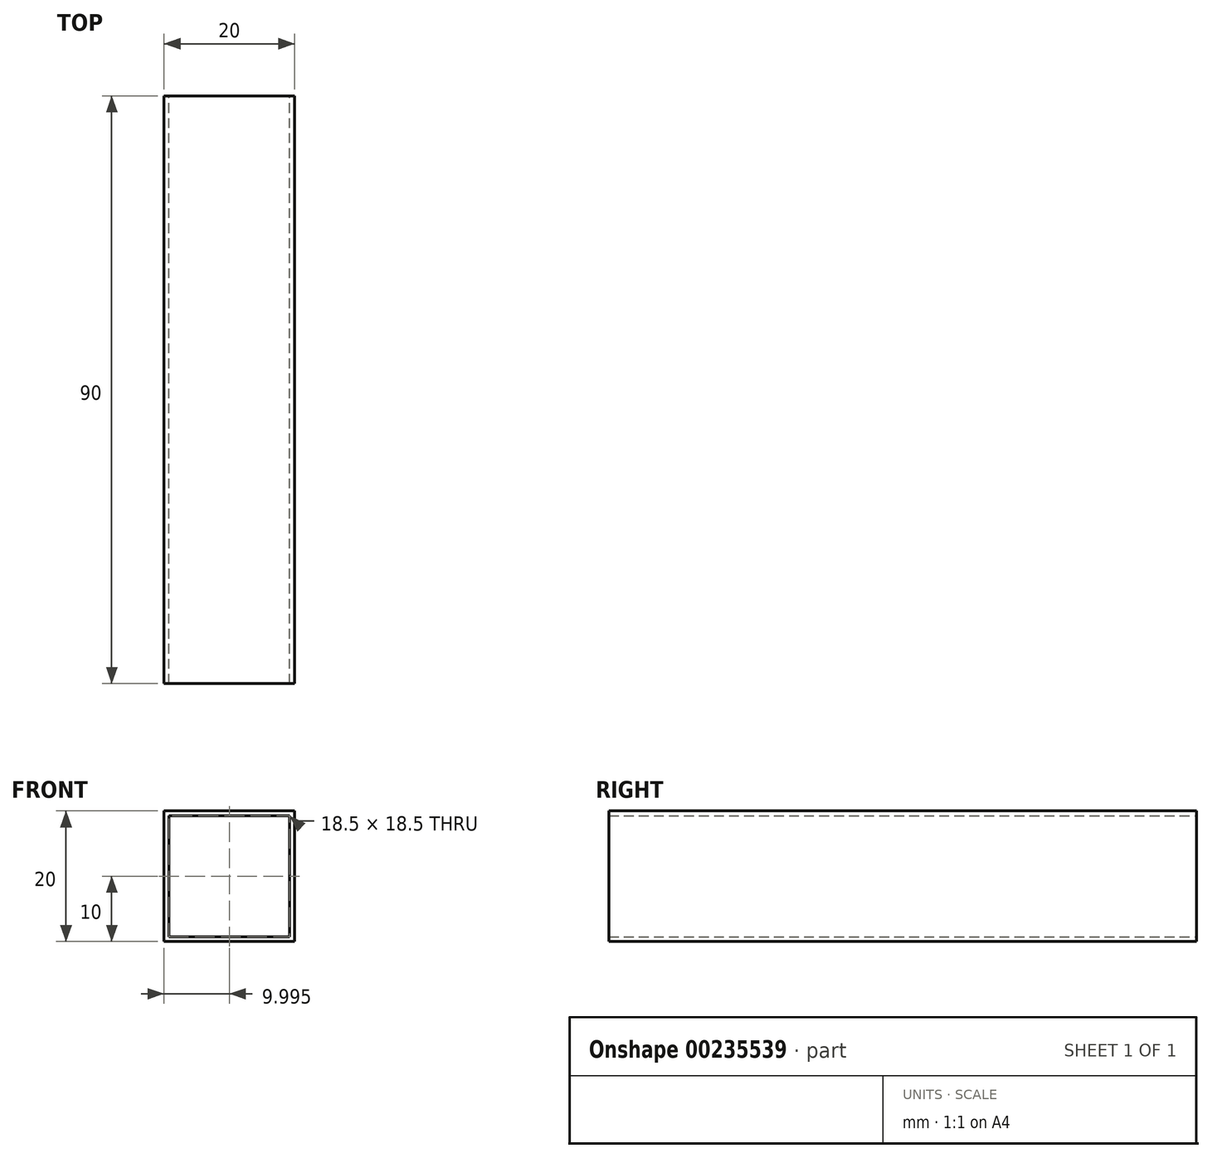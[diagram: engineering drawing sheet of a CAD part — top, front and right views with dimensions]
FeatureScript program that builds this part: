
annotation { "Feature Type Name" : "Feature", "Feature Type Description" : "" }
export const myFeature = defineFeature(function(context is Context, id is Id, definition is map)
    precondition{}
    {
        {
            var Q0;
            Q0=qCreatedBy(makeId("Front.planeOp"),FACE);
            var sketch = newSketch(context, id + "F0", { "sketchPlane" : qUnion([Q0])});
            skLineSegment(sketch, "E0.bottom", {"start": v(-34.48, 27) * mm, "end": v(-54.48, 27) * mm});
            skLineSegment(sketch, "E0.top", {"start": v(-34.48, 47) * mm, "end": v(-54.48, 47) * mm});
            skLineSegment(sketch, "E0.left", {"start": v(-34.48, 27) * mm, "end": v(-34.48, 47) * mm});
            skLineSegment(sketch, "E0.right", {"start": v(-54.48, 27) * mm, "end": v(-54.48, 47) * mm});
            skPoint(sketch, "E0.middle", {"position": v(-44.48, 37) * mm});
            skLineSegment(sketch, "E1.bottom", {"start": v(-35.23, 27.75) * mm, "end": v(-53.73, 27.75) * mm});
            skLineSegment(sketch, "E1.top", {"start": v(-35.23, 46.25) * mm, "end": v(-53.73, 46.25) * mm});
            skLineSegment(sketch, "E1.left", {"start": v(-35.23, 27.75) * mm, "end": v(-35.23, 46.25) * mm});
            skLineSegment(sketch, "E1.right", {"start": v(-53.73, 27.75) * mm, "end": v(-53.73, 46.25) * mm});
            skSolve(sketch);
        }
        {
            var Q0;
            Q0=makeQuery(id+"F0.imprint","IMPRINT",FACE,{"disambiguationData":[TD([[makeQuery(id+"F0.imprint","IMPRINT",EDGE,{"derivedFrom":sQuery(id+"F0.wireOp",EDGE,"E0.bottom")}),-1.0]])]});
            extrude(context, id + "F1", {"entities" : qUnion([Q0]), "depth" : 90 * mm});
        }
    });
